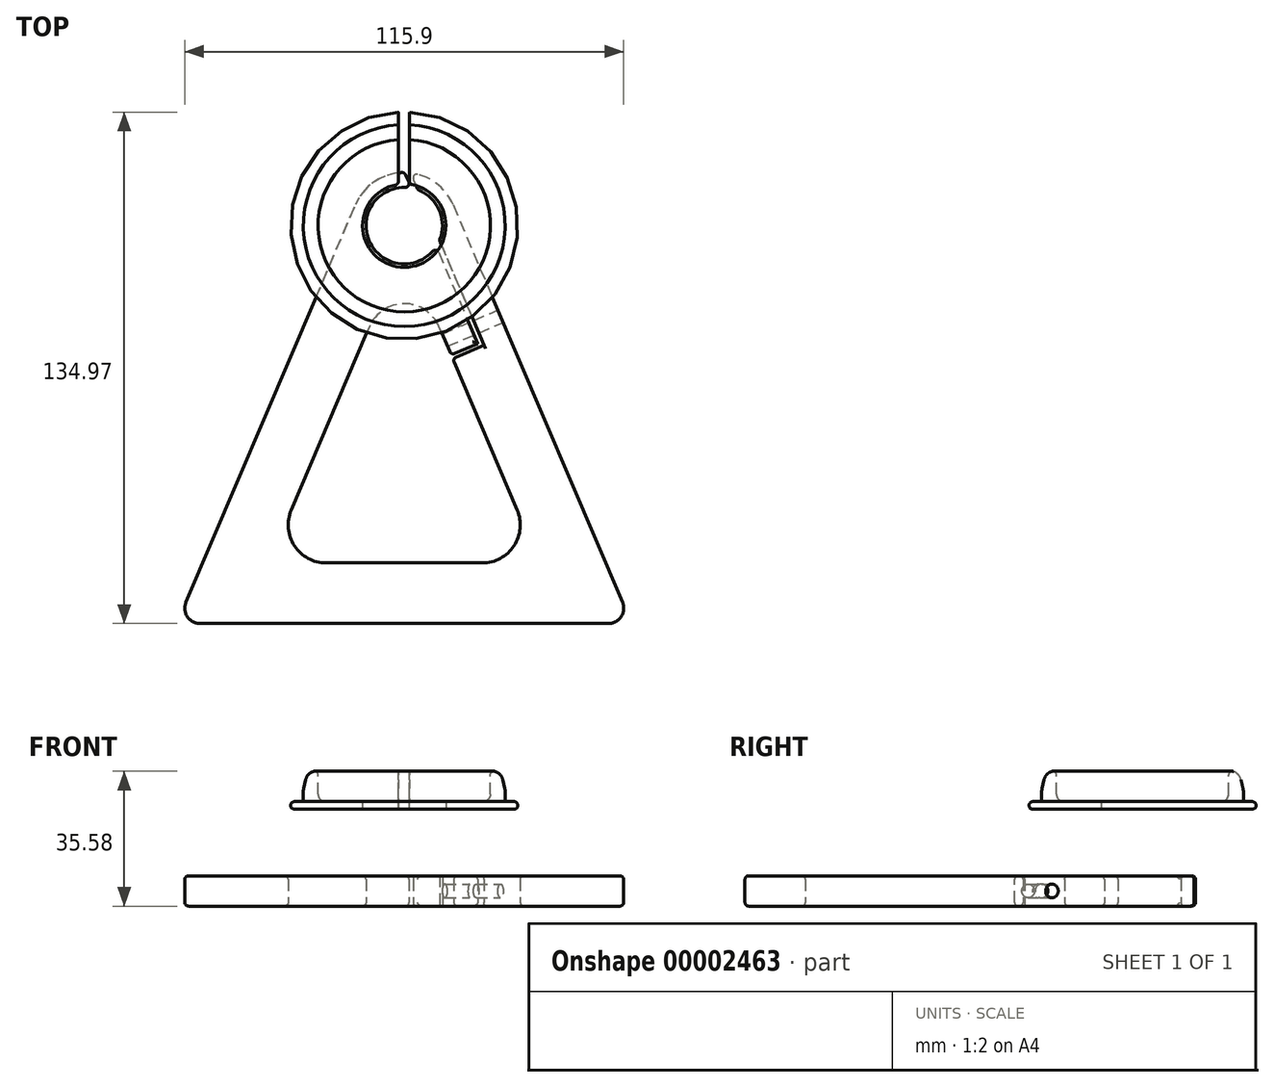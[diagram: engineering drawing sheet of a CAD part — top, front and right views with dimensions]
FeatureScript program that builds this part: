
annotation { "Feature Type Name" : "Feature", "Feature Type Description" : "" }
export const myFeature = defineFeature(function(context is Context, id is Id, definition is map)
    precondition{}
    {
        {
            var Q0;
            Q0=qCreatedBy(makeId("Top.planeOp"),FACE);
            var sketch = newSketch(context, id + "F0", { "sketchPlane" : qUnion([Q0])});
            skLineSegment(sketch, "E0", {"start": v(-53.95, -105) * mm, "end": v(53.95, -105) * mm});
            skArc(sketch, "E1", {"start": v(9.3, -3.95) * mm, "mid": v(-8.9, 4.76) * mm, "end": v(8.45, -5.53) * mm});
            skLineSegment(sketch, "E2", {"start": v(-57.62, -99.43) * mm, "end": v(-12.88, 5.5) * mm});
            skLineSegment(sketch, "E3", {"start": v(12.88, 5.5) * mm, "end": v(57.62, -99.43) * mm});
            skArc(sketch, "E4", {"start": v(12.88, 5.5) * mm, "mid": v(0, 14) * mm, "end": v(-12.88, 5.5) * mm});
            skPoint(sketch, "E5.visualSharp", {"position": v(-60, -105) * mm});
            skArc(sketch, "E5.filletArc", {"start": v(-57.62, -99.43) * mm, "mid": v(-57.28, -103.2) * mm, "end": v(-53.95, -105) * mm});
            skPoint(sketch, "E6.visualSharp", {"position": v(60, -105) * mm});
            skArc(sketch, "E6.filletArc", {"start": v(53.95, -105) * mm, "mid": v(57.28, -103.2) * mm, "end": v(57.62, -99.43) * mm});
            skLineSegment(sketch, "E7", {"start": v(-9.2, -26.67) * mm, "end": v(-29.84, -75.08) * mm});
            skLineSegment(sketch, "E8", {"start": v(-20.65, -89) * mm, "end": v(20.65, -89) * mm});
            skLineSegment(sketch, "E9", {"start": v(29.84, -75.08) * mm, "end": v(9.2, -26.67) * mm});
            skArc(sketch, "E10.filletArc", {"start": v(9.2, -26.67) * mm, "mid": v(0, -20.59) * mm, "end": v(-9.2, -26.67) * mm});
            skPoint(sketch, "E11.visualSharp", {"position": v(-35.78, -89) * mm});
            skArc(sketch, "E11.filletArc", {"start": v(-29.84, -75.08) * mm, "mid": v(-28.99, -84.51) * mm, "end": v(-20.65, -89) * mm});
            skPoint(sketch, "E12.visualSharp", {"position": v(35.78, -89) * mm});
            skArc(sketch, "E12.filletArc", {"start": v(20.65, -89) * mm, "mid": v(28.99, -84.51) * mm, "end": v(29.84, -75.08) * mm});
            skCircle(sketch, "E13", {"center": v(0, 0) * mm, "radius": 100 * mm, "construction": true});
            skLineSegment(sketch, "E14", {"start": v(1.68, 13.9) * mm, "end": v(21.06, -31.55) * mm});
            skLineSegment(sketch, "E15", {"start": v(0.12, 14) * mm, "end": v(19.39, -31.17) * mm});
            skLineSegment(sketch, "E16", {"start": v(12.79, -35.08) * mm, "end": v(21.06, -31.55) * mm});
            skLineSegment(sketch, "E17", {"start": v(12.4, -34.16) * mm, "end": v(19.39, -31.17) * mm});
            skCircle(sketch, "E18", {"center": v(40, -91.8) * mm, "radius": 13.2 * mm, "construction": true});
            skCircle(sketch, "E19", {"center": v(40, -91.8) * mm, "radius": 10 * mm, "construction": true});
            skCircle(sketch, "E20", {"center": v(-40, -91.8) * mm, "radius": 13.2 * mm, "construction": true});
            skCircle(sketch, "E21", {"center": v(-40, -91.8) * mm, "radius": 10.2 * mm, "construction": true});
            skSolve(sketch);
        }
        {
            var Q0;
            Q0=makeQuery(id+"F0.imprint","IMPRINT",FACE,{"disambiguationData":[TD([[makeQuery(id+"F0.imprint","IMPRINT",EDGE,{"derivedFrom":sQuery(id+"F0.wireOp",EDGE,"E0")}),1.0]])]});
            extrude(context, id + "F1", {"entities" : qUnion([Q0]), "depth" : 8 * mm});
        }
        {
            var Q0;
            Q0=makeQuery(id+"F1.opExtrude","SWEPT_FACE",FACE,{"disambiguationData":[OSD([sQuery(id+"F0.wireOp",EDGE,"E3")])]});
            var sketch = newSketch(context, id + "F2", { "sketchPlane" : qUnion([Q0])});
            skCircle(sketch, "E22", {"center": v(-32, 4) * mm, "radius": 1.8 * mm});
            skSolve(sketch);
        }
        {
            var Q0;
            Q0=qSketchRegion(id+"F2",true);
            var Q1;
            {var subQ0=sQuery(id+"F0.wireOp",EDGE,"E9");Q1=makeQuery(id+"F1.opExtrude","SWEPT_FACE",FACE,{"disambiguationData":[OSD([subQ0]),TDD([makeQuery(id+"F0.imprint","IMPRINT",EDGE,{"disambiguationData":[TD([[makeQuery(id+"F0.imprint","INTERSECT",VERTEX,{"derivedFrom":[subQ0,sQuery(id+"F0.wireOp",EDGE,"E10.filletArc")]}),1.0]])],"derivedFrom":subQ0})])]});}
            extrude(context, id + "F3", {"entities" : qUnion([Q0]), "operationType" : NewBodyOperationType.REMOVE, "endBound" : BoundingType.UP_TO_SURFACE, "oppositeDirection" : true, "endBoundEntityFace" : qUnion([Q1]), "depth" : 25 * mm});
        }
        {
            var Q0;
            {var subQ0=sQuery(id+"F0.wireOp",EDGE,"E1");var subQ1=sQuery(id+"F0.wireOp",EDGE,"E15");Q0=makeQuery(id+"F1.opExtrude","CAP_EDGE",EDGE,{"disambiguationData":[OSD([subQ0]),TDD([makeQuery(id+"F0.imprint","IMPRINT",EDGE,{"disambiguationData":[TD([[makeQuery(id+"F0.imprint","INTERSECT",VERTEX,{"disambiguationData":[OD(0.0)],"derivedFrom":[subQ0,subQ1]}),1.0]])],"derivedFrom":subQ0})])],"isStart":false});}
            var Q1;
            {var subQ0=sQuery(id+"F0.wireOp",EDGE,"E4");Q1=makeQuery(id+"F1.opExtrude","CAP_EDGE",EDGE,{"disambiguationData":[OSD([subQ0]),TDD([makeQuery(id+"F0.imprint","IMPRINT",EDGE,{"disambiguationData":[TD([[makeQuery(id+"F0.imprint","INTERSECT",VERTEX,{"derivedFrom":[sQuery(id+"F0.wireOp",EDGE,"E2"),subQ0]}),1.0]])],"derivedFrom":subQ0})])],"isStart":false});}
            var Q2;
            {var subQ0=sQuery(id+"F0.wireOp",EDGE,"E15");Q2=makeQuery(id+"F1.opExtrude","CAP_EDGE",EDGE,{"disambiguationData":[OSD([subQ0]),TDD([makeQuery(id+"F0.imprint","IMPRINT",EDGE,{"disambiguationData":[TD([[makeQuery(id+"F0.imprint","INTERSECT",VERTEX,{"disambiguationData":[OD(0.0)],"derivedFrom":[sQuery(id+"F0.wireOp",EDGE,"E1"),subQ0]}),-1.0]])],"derivedFrom":subQ0})])],"isStart":false});}
            var Q3;
            Q3=makeQuery(id+"F1.opExtrude","CAP_EDGE",EDGE,{"disambiguationData":[OSD([sQuery(id+"F0.wireOp",EDGE,"E17")])],"isStart":false});
            var Q4;
            Q4=makeQuery(id+"F1.opExtrude","CAP_EDGE",EDGE,{"disambiguationData":[OSD([sQuery(id+"F0.wireOp",EDGE,"E10.filletArc")])],"isStart":false});
            var Q5;
            {var subQ0=sQuery(id+"F0.wireOp",EDGE,"E9");Q5=makeQuery(id+"F1.opExtrude","CAP_EDGE",EDGE,{"disambiguationData":[OSD([subQ0]),TDD([makeQuery(id+"F0.imprint","IMPRINT",EDGE,{"disambiguationData":[TD([[makeQuery(id+"F0.imprint","INTERSECT",VERTEX,{"derivedFrom":[subQ0,sQuery(id+"F0.wireOp",EDGE,"E10.filletArc")]}),1.0]])],"derivedFrom":subQ0})])],"isStart":false});}
            var Q6;
            {var subQ0=sQuery(id+"F0.wireOp",EDGE,"E1");var subQ1=sQuery(id+"F0.wireOp",EDGE,"E14");Q6=makeQuery(id+"F1.opExtrude","CAP_EDGE",EDGE,{"disambiguationData":[OSD([subQ0]),TDD([makeQuery(id+"F0.imprint","IMPRINT",EDGE,{"disambiguationData":[TD([[makeQuery(id+"F0.imprint","INTERSECT",VERTEX,{"disambiguationData":[OD(0.0)],"derivedFrom":[subQ0,subQ1]}),-1.0]])],"derivedFrom":subQ0})])],"isStart":false});}
            var Q7;
            {var subQ0=sQuery(id+"F0.wireOp",EDGE,"E1");var subQ1=sQuery(id+"F0.wireOp",EDGE,"E15");Q7=makeQuery(id+"F1.opExtrude","CAP_EDGE",EDGE,{"disambiguationData":[OSD([subQ0]),TDD([makeQuery(id+"F0.imprint","IMPRINT",EDGE,{"disambiguationData":[TD([[makeQuery(id+"F0.imprint","INTERSECT",VERTEX,{"disambiguationData":[OD(0.0)],"derivedFrom":[subQ0,subQ1]}),1.0]])],"derivedFrom":subQ0})])],"isStart":true});}
            var Q8;
            {var subQ0=sQuery(id+"F0.wireOp",EDGE,"E15");Q8=makeQuery(id+"F1.opExtrude","CAP_EDGE",EDGE,{"disambiguationData":[OSD([subQ0]),TDD([makeQuery(id+"F0.imprint","IMPRINT",EDGE,{"disambiguationData":[TD([[makeQuery(id+"F0.imprint","INTERSECT",VERTEX,{"disambiguationData":[OD(0.0)],"derivedFrom":[sQuery(id+"F0.wireOp",EDGE,"E1"),subQ0]}),-1.0]])],"derivedFrom":subQ0})])],"isStart":true});}
            var Q9;
            Q9=makeQuery(id+"F1.opExtrude","CAP_EDGE",EDGE,{"disambiguationData":[OSD([sQuery(id+"F0.wireOp",EDGE,"E17")])],"isStart":true});
            var Q10;
            {var subQ0=sQuery(id+"F0.wireOp",EDGE,"E9");Q10=makeQuery(id+"F1.opExtrude","CAP_EDGE",EDGE,{"disambiguationData":[OSD([subQ0]),TDD([makeQuery(id+"F0.imprint","IMPRINT",EDGE,{"disambiguationData":[TD([[makeQuery(id+"F0.imprint","INTERSECT",VERTEX,{"derivedFrom":[subQ0,sQuery(id+"F0.wireOp",EDGE,"E10.filletArc")]}),1.0]])],"derivedFrom":subQ0})])],"isStart":true});}
            var Q11;
            {var subQ0=sQuery(id+"F0.wireOp",EDGE,"E14");Q11=makeQuery(id+"F1.opExtrude","CAP_EDGE",EDGE,{"disambiguationData":[OSD([subQ0]),TDD([makeQuery(id+"F0.imprint","IMPRINT",EDGE,{"disambiguationData":[TD([[makeQuery(id+"F0.imprint","INTERSECT",VERTEX,{"disambiguationData":[OD(0.0)],"derivedFrom":[sQuery(id+"F0.wireOp",EDGE,"E1"),subQ0]}),-1.0]])],"derivedFrom":subQ0})])],"isStart":true});}
            var Q12;
            Q12=makeQuery(id+"F1.opExtrude","CAP_EDGE",EDGE,{"disambiguationData":[OSD([sQuery(id+"F0.wireOp",EDGE,"E16")])],"isStart":true});
            var Q13;
            Q13=makeQuery(id+"F1.opExtrude","CAP_EDGE",EDGE,{"disambiguationData":[OSD([sQuery(id+"F0.wireOp",EDGE,"E3")])],"isStart":true});
            var Q14;
            {var subQ0=sQuery(id+"F0.wireOp",EDGE,"E1");var subQ1=sQuery(id+"F0.wireOp",EDGE,"E14");Q14=makeQuery(id+"F1.opExtrude","CAP_EDGE",EDGE,{"disambiguationData":[OSD([subQ0]),TDD([makeQuery(id+"F0.imprint","IMPRINT",EDGE,{"disambiguationData":[TD([[makeQuery(id+"F0.imprint","INTERSECT",VERTEX,{"disambiguationData":[OD(0.0)],"derivedFrom":[subQ0,subQ1]}),-1.0]])],"derivedFrom":subQ0})])],"isStart":true});}
            var Q15;
            {var subQ0=sQuery(id+"F0.wireOp",EDGE,"E1");var subQ1=sQuery(id+"F0.wireOp",EDGE,"E15");Q15=makeQuery(id+"F1.opExtrude","SWEPT_EDGE",EDGE,{"disambiguationData":[OSD([subQ0,subQ1]),TDD([makeQuery(id+"F0.imprint","INTERSECT",VERTEX,{"disambiguationData":[OD(0.0)],"derivedFrom":[subQ0,subQ1]})])]});}
            var Q16;
            {var subQ0=sQuery(id+"F0.wireOp",EDGE,"E1");var subQ1=sQuery(id+"F0.wireOp",EDGE,"E15");Q16=makeQuery(id+"F1.opExtrude","SWEPT_EDGE",EDGE,{"disambiguationData":[OSD([subQ0,subQ1]),TDD([makeQuery(id+"F0.imprint","INTERSECT",VERTEX,{"disambiguationData":[OD(1.0)],"derivedFrom":[subQ0,subQ1]})])]});}
            var Q17;
            Q17=makeQuery(id+"F1.opExtrude","SWEPT_EDGE",EDGE,{"disambiguationData":[OSD([sQuery(id+"F0.wireOp",EDGE,"E4"),sQuery(id+"F0.wireOp",EDGE,"E15")])]});
            var Q18;
            {var subQ0=sQuery(id+"F0.wireOp",EDGE,"E15");Q18=makeQuery(id+"F1.opExtrude","CAP_EDGE",EDGE,{"disambiguationData":[OSD([subQ0]),TDD([makeQuery(id+"F0.imprint","IMPRINT",EDGE,{"disambiguationData":[TD([[makeQuery(id+"F0.imprint","INTERSECT",VERTEX,{"derivedFrom":[sQuery(id+"F0.wireOp",EDGE,"E4"),subQ0]}),-1.0]])],"derivedFrom":subQ0})])],"isStart":false});}
            var Q19;
            {var subQ0=sQuery(id+"F0.wireOp",EDGE,"E14");Q19=makeQuery(id+"F1.opExtrude","CAP_EDGE",EDGE,{"disambiguationData":[OSD([subQ0]),TDD([makeQuery(id+"F0.imprint","IMPRINT",EDGE,{"disambiguationData":[TD([[makeQuery(id+"F0.imprint","INTERSECT",VERTEX,{"derivedFrom":[sQuery(id+"F0.wireOp",EDGE,"E4"),subQ0]}),-1.0]])],"derivedFrom":subQ0})])],"isStart":false});}
            var Q20;
            Q20=makeQuery(id+"F1.opExtrude","SWEPT_EDGE",EDGE,{"disambiguationData":[OSD([sQuery(id+"F0.wireOp",EDGE,"E4"),sQuery(id+"F0.wireOp",EDGE,"E14")])]});
            var Q21;
            {var subQ0=sQuery(id+"F0.wireOp",EDGE,"E14");Q21=makeQuery(id+"F1.opExtrude","CAP_EDGE",EDGE,{"disambiguationData":[OSD([subQ0]),TDD([makeQuery(id+"F0.imprint","IMPRINT",EDGE,{"disambiguationData":[TD([[makeQuery(id+"F0.imprint","INTERSECT",VERTEX,{"disambiguationData":[OD(0.0)],"derivedFrom":[sQuery(id+"F0.wireOp",EDGE,"E1"),subQ0]}),-1.0]])],"derivedFrom":subQ0})])],"isStart":false});}
            var Q22;
            {var subQ0=sQuery(id+"F0.wireOp",EDGE,"E1");var subQ1=sQuery(id+"F0.wireOp",EDGE,"E14");Q22=makeQuery(id+"F1.opExtrude","SWEPT_EDGE",EDGE,{"disambiguationData":[OSD([subQ0,subQ1]),TDD([makeQuery(id+"F0.imprint","INTERSECT",VERTEX,{"disambiguationData":[OD(0.0)],"derivedFrom":[subQ0,subQ1]})])]});}
            var Q23;
            {var subQ0=sQuery(id+"F0.wireOp",EDGE,"E15");Q23=makeQuery(id+"F1.opExtrude","CAP_EDGE",EDGE,{"disambiguationData":[OSD([subQ0]),TDD([makeQuery(id+"F0.imprint","IMPRINT",EDGE,{"disambiguationData":[TD([[makeQuery(id+"F0.imprint","INTERSECT",VERTEX,{"derivedFrom":[sQuery(id+"F0.wireOp",EDGE,"E4"),subQ0]}),-1.0]])],"derivedFrom":subQ0})])],"isStart":true});}
            var Q24;
            {var subQ0=sQuery(id+"F0.wireOp",EDGE,"E14");Q24=makeQuery(id+"F1.opExtrude","CAP_EDGE",EDGE,{"disambiguationData":[OSD([subQ0]),TDD([makeQuery(id+"F0.imprint","IMPRINT",EDGE,{"disambiguationData":[TD([[makeQuery(id+"F0.imprint","INTERSECT",VERTEX,{"derivedFrom":[sQuery(id+"F0.wireOp",EDGE,"E4"),subQ0]}),-1.0]])],"derivedFrom":subQ0})])],"isStart":true});}
            var Q25;
            {var subQ0=sQuery(id+"F0.wireOp",EDGE,"E1");var subQ1=sQuery(id+"F0.wireOp",EDGE,"E14");Q25=makeQuery(id+"F1.opExtrude","SWEPT_EDGE",EDGE,{"disambiguationData":[OSD([subQ0,subQ1]),TDD([makeQuery(id+"F0.imprint","INTERSECT",VERTEX,{"disambiguationData":[OD(1.0)],"derivedFrom":[subQ0,subQ1]})])]});}
            var Q26;
            Q26=makeQuery(id+"F1.opExtrude","CAP_EDGE",EDGE,{"disambiguationData":[OSD([sQuery(id+"F0.wireOp",EDGE,"E16")])],"isStart":false});
            var Q27;
            Q27=makeQuery(id+"F1.opExtrude","SWEPT_EDGE",EDGE,{"disambiguationData":[OSD([sQuery(id+"F0.wireOp",EDGE,"E9"),sQuery(id+"F0.wireOp",EDGE,"E16")])]});
            var Q28;
            Q28=makeQuery(id+"F1.opExtrude","SWEPT_EDGE",EDGE,{"disambiguationData":[OSD([sQuery(id+"F0.wireOp",EDGE,"E9"),sQuery(id+"F0.wireOp",EDGE,"E17")])]});
            fillet(context, id + "F4", {"entities" : qUnion([Q0, Q1, Q2, Q3, Q4, Q5, Q6, Q7, Q8, Q9, Q10, Q11, Q12, Q13, Q14, Q15, Q16, Q17, Q18, Q19, Q20, Q21, Q22, Q23, Q24, Q25, Q26, Q27, Q28]), "radius" : 1 * mm, "tangentPropagation" : true, "allowEdgeOverflow" : false});
        }
        {
            var Q0;
            Q0=makeQuery(id+"F3.boolean.opBoolean","COPY",EDGE,{"derivedFrom":makeQuery(id+"F3.opExtrude","CAP_EDGE",EDGE,{"disambiguationData":[OSD([sQuery(id+"F2.wireOp",EDGE,"E22")])],"isStart":true})});
            var Q1;
            {var subQ0=sQuery(id+"F0.wireOp",EDGE,"E14");Q1=makeQuery(id+"F3.boolean.opBoolean","INTERSECT",EDGE,{"derivedFrom":[makeQuery(id+"F1.opExtrude","SWEPT_FACE",FACE,{"disambiguationData":[OSD([subQ0]),TDD([makeQuery(id+"F0.imprint","IMPRINT",EDGE,{"disambiguationData":[TD([[makeQuery(id+"F0.imprint","INTERSECT",VERTEX,{"disambiguationData":[OD(0.0)],"derivedFrom":[sQuery(id+"F0.wireOp",EDGE,"E1"),subQ0]}),-1.0]])],"derivedFrom":subQ0})])]}),makeQuery(id+"F3.opExtrude","SWEPT_FACE",FACE,{"disambiguationData":[OSD([sQuery(id+"F2.wireOp",EDGE,"E22")])]})]});}
            var Q2;
            {var subQ0=sQuery(id+"F0.wireOp",EDGE,"E15");Q2=makeQuery(id+"F3.boolean.opBoolean","INTERSECT",EDGE,{"derivedFrom":[makeQuery(id+"F1.opExtrude","SWEPT_FACE",FACE,{"disambiguationData":[OSD([subQ0]),TDD([makeQuery(id+"F0.imprint","IMPRINT",EDGE,{"disambiguationData":[TD([[makeQuery(id+"F0.imprint","INTERSECT",VERTEX,{"disambiguationData":[OD(0.0)],"derivedFrom":[sQuery(id+"F0.wireOp",EDGE,"E1"),subQ0]}),-1.0]])],"derivedFrom":subQ0})])]}),makeQuery(id+"F3.opExtrude","SWEPT_FACE",FACE,{"disambiguationData":[OSD([sQuery(id+"F2.wireOp",EDGE,"E22")])]})]});}
            var Q3;
            Q3=makeQuery(id+"F3.boolean.opBoolean","COPY",EDGE,{"derivedFrom":makeQuery(id+"F3.opExtrude","CAP_EDGE",EDGE,{"disambiguationData":[OSD([sQuery(id+"F2.wireOp",EDGE,"E22")])],"isStart":false})});
            fillet(context, id + "F5", {"entities" : qUnion([Q0, Q1, Q2, Q3]), "radius" : 0.6 * mm, "tangentPropagation" : true, "allowEdgeOverflow" : false});
        }
        {
            var Q0;
            Q0=qCreatedBy(makeId("Right.planeOp"),FACE);
            var sketch = newSketch(context, id + "F6", { "sketchPlane" : qUnion([Q0])});
            skLineSegment(sketch, "E23", {"start": v(29, 25.58) * mm, "end": v(0, 25.58) * mm});
            skPoint(sketch, "E24.visualSharp", {"position": v(24.99, 35.56) * mm});
            skArc(sketch, "E24.filletArc", {"start": v(26.02, 33.34) * mm, "mid": v(25.32, 34.7) * mm, "end": v(24.04, 35.53) * mm});
            skLineSegment(sketch, "E25", {"start": v(0, 30.58) * mm, "end": v(26.65, 30.58) * mm, "construction": true});
            skArc(sketch, "E26", {"start": v(24.04, 35.53) * mm, "mid": v(23.15, 35.4) * mm, "end": v(22.74, 34.6) * mm});
            skLineSegment(sketch, "E27", {"start": v(26.58, 35.58) * mm, "end": v(20.64, 35.58) * mm, "construction": true});
            skLineSegment(sketch, "E28.bottom", {"start": v(27.45, 27.58) * mm, "end": v(29, 27.58) * mm});
            skPoint(sketch, "E29.visualSharp", {"position": v(23.1, 27.58) * mm});
            skArc(sketch, "E29.filletArc", {"start": v(26.65, 28.38) * mm, "mid": v(26.88, 27.81) * mm, "end": v(27.45, 27.58) * mm});
            skArc(sketch, "E30", {"start": v(29, 25.58) * mm, "mid": v(30, 26.58) * mm, "end": v(29, 27.58) * mm});
            skLineSegment(sketch, "E31", {"start": v(20.74, 27.58) * mm, "end": v(0, 27.58) * mm});
            skLineSegment(sketch, "E32", {"start": v(0, 27.58) * mm, "end": v(0, 25.58) * mm});
            skLineSegment(sketch, "E33", {"start": v(22.74, 34.6) * mm, "end": v(22.74, 29.58) * mm});
            skLineSegment(sketch, "E34", {"start": v(23.73, 34.6) * mm, "end": v(22.74, 34.6) * mm, "construction": true});
            skPoint(sketch, "E35.visualSharp", {"position": v(22.74, 27.58) * mm});
            skArc(sketch, "E35.filletArc", {"start": v(20.74, 27.58) * mm, "mid": v(22.15, 28.16) * mm, "end": v(22.74, 29.58) * mm});
            skLineSegment(sketch, "E36", {"start": v(26.65, 28.38) * mm, "end": v(26.65, 30.13) * mm});
            skLineSegment(sketch, "E37", {"start": v(26.02, 33.34) * mm, "end": v(26.55, 31.02) * mm});
            skPoint(sketch, "E38.visualSharp", {"position": v(26.65, 30.58) * mm});
            skArc(sketch, "E38.filletArc", {"start": v(26.65, 30.13) * mm, "mid": v(26.63, 30.57) * mm, "end": v(26.55, 31.02) * mm});
            skSolve(sketch);
        }
        {
            var Q0;
            Q0=qSketchRegion(id+"F6",true);
            var Q1;
            Q1=sQuery(id+"F6.wireOp",EDGE,"E32");
            revolve(context, id + "F7", {"entities" : qUnion([Q0]), "axis" : qUnion([Q1]), "revolveType" : RevolveType.FULL});
        }
        {
            var Q0;
            Q0=makeQuery(id+"F7.opRevolve","SWEPT_FACE",FACE,{"disambiguationData":[OSD([sQuery(id+"F6.wireOp",EDGE,"E23")])]});
            var sketch = newSketch(context, id + "F8", { "sketchPlane" : qUnion([Q0])});
            skCircle(sketch, "E39", {"center": v(0, 0) * mm, "radius": 11 * mm});
            skLineSegment(sketch, "E40.rect.top", {"start": v(1.41, -38.94) * mm, "end": v(-1.59, -38.94) * mm});
            skLineSegment(sketch, "E40.rect.left", {"start": v(1.41, -10.9) * mm, "end": v(1.41, -38.94) * mm});
            skLineSegment(sketch, "E40.rect.right", {"start": v(-1.59, -10.88) * mm, "end": v(-1.59, -38.94) * mm});
            skPoint(sketch, "E40.rect.middle", {"position": v(0, -36.15) * mm});
            skSolve(sketch);
        }
        {
            var Q0;
            Q0=qSketchRegion(id+"F8",true);
            var Q1;
            Q1=makeQuery(id+"F7.opRevolve","SWEPT_FACE",FACE,{"disambiguationData":[OSD([sQuery(id+"F6.wireOp",EDGE,"E23")])]});
            extrude(context, id + "F9", {"entities" : qUnion([Q0]), "operationType" : NewBodyOperationType.REMOVE, "endBound" : BoundingType.UP_TO_BODY, "oppositeDirection" : true, "endBoundEntityBody" : qUnion([Q1]), "depth" : 25 * mm});
        }
        {
            var Q0;
            Q0=makeQuery(id+"F9.boolean.opBoolean","COPY",EDGE,{"derivedFrom":makeQuery(id+"F9.opExtrude","CAP_EDGE",EDGE,{"disambiguationData":[OSD([sQuery(id+"F8.wireOp",EDGE,"E39")])],"isStart":false})});
            var Q1;
            Q1=makeQuery(id+"F9.boolean.opBoolean","COPY",EDGE,{"derivedFrom":makeQuery(id+"F9.opExtrude","CAP_EDGE",EDGE,{"disambiguationData":[OSD([sQuery(id+"F8.wireOp",EDGE,"E40.rect.right")]),topologyDisambiguationEdgeConnected([makeQuery(id+"F7.opRevolve","SWEPT_FACE",FACE,{"disambiguationData":[OSD([sQuery(id+"F6.wireOp",EDGE,"E31")])]})])],"isStart":false})});
            var Q2;
            Q2=makeQuery(id+"F9.boolean.opBoolean","COPY",EDGE,{"derivedFrom":makeQuery(id+"F9.opExtrude","CAP_EDGE",EDGE,{"disambiguationData":[OSD([sQuery(id+"F8.wireOp",EDGE,"E40.rect.right")]),topologyDisambiguationEdgeConnected([makeQuery(id+"F7.opRevolve","SWEPT_FACE",FACE,{"disambiguationData":[OSD([sQuery(id+"F6.wireOp",EDGE,"E26")])]})])],"isStart":false})});
            var Q3;
            Q3=makeQuery(id+"F9.boolean.opBoolean","COPY",EDGE,{"derivedFrom":makeQuery(id+"F9.opExtrude","CAP_EDGE",EDGE,{"disambiguationData":[OSD([sQuery(id+"F8.wireOp",EDGE,"E40.rect.left")]),topologyDisambiguationEdgeConnected([makeQuery(id+"F7.opRevolve","SWEPT_FACE",FACE,{"disambiguationData":[OSD([sQuery(id+"F6.wireOp",EDGE,"E31")])]})])],"isStart":false})});
            var Q4;
            {var subQ0=sQuery(id+"F8.wireOp",EDGE,"E40.rect.left");Q4=makeQuery(id+"F9.boolean.opBoolean","COPY",EDGE,{"derivedFrom":makeQuery(id+"F9.opExtrude","TWEAK_EDGE",EDGE,{"derivedFrom":[makeQuery(id+"F7.opRevolve","SWEPT_FACE",FACE,{"disambiguationData":[OSD([sQuery(id+"F6.wireOp",EDGE,"a11749e0-a4c9-4a4f-9974-4c692c2e9dff.5")])]}),makeQuery(id+"F8.imprint","IMPRINT",EDGE,{"disambiguationData":[TD([[makeQuery(id+"F8.imprint","INTERSECT",VERTEX,{"derivedFrom":[sQuery(id+"F8.wireOp",EDGE,"E39"),subQ0]}),-1.0]])],"derivedFrom":subQ0}),makeQuery(id+"F8.imprint","IMPRINT",EDGE,{"disambiguationData":[TD([[makeQuery(id+"F8.imprint","INTERSECT",VERTEX,{"derivedFrom":[sQuery(id+"F8.wireOp",EDGE,"E40.rect.top"),subQ0]}),1.0]])],"derivedFrom":subQ0})]})});}
            var Q5;
            Q5=makeQuery(id+"F9.boolean.opBoolean","COPY",EDGE,{"derivedFrom":makeQuery(id+"F9.opExtrude","CAP_EDGE",EDGE,{"disambiguationData":[OSD([sQuery(id+"F8.wireOp",EDGE,"E40.rect.left")]),topologyDisambiguationEdgeConnected([makeQuery(id+"F7.opRevolve","SWEPT_FACE",FACE,{"disambiguationData":[OSD([sQuery(id+"F6.wireOp",EDGE,"E26")])]})])],"isStart":false})});
            var Q6;
            Q6=makeQuery(id+"F9.boolean.opBoolean","COPY",EDGE,{"derivedFrom":makeQuery(id+"F9.opExtrude","CAP_EDGE",EDGE,{"disambiguationData":[OSD([sQuery(id+"F8.wireOp",EDGE,"E40.rect.left")]),topologyDisambiguationEdgeConnected([makeQuery(id+"F7.opRevolve","SWEPT_FACE",FACE,{"disambiguationData":[OSD([sQuery(id+"F6.wireOp",EDGE,"E28.bottom")])]})])],"isStart":false})});
            var Q7;
            Q7=makeQuery(id+"F9.boolean.opBoolean","COPY",EDGE,{"derivedFrom":makeQuery(id+"F9.opExtrude","SWEPT_EDGE",EDGE,{"disambiguationData":[OSD([sQuery(id+"F8.wireOp",EDGE,"E39"),sQuery(id+"F8.wireOp",EDGE,"E40.rect.left")])]})});
            var Q8;
            Q8=makeQuery(id+"F9.boolean.opBoolean","COPY",EDGE,{"derivedFrom":makeQuery(id+"F9.opExtrude","SWEPT_EDGE",EDGE,{"disambiguationData":[OSD([sQuery(id+"F8.wireOp",EDGE,"E39"),sQuery(id+"F8.wireOp",EDGE,"E40.rect.right")])]})});
            var Q9;
            Q9=makeQuery(id+"F9.boolean.opBoolean","COPY",EDGE,{"derivedFrom":makeQuery(id+"F9.opExtrude","CAP_EDGE",EDGE,{"disambiguationData":[OSD([sQuery(id+"F8.wireOp",EDGE,"E39")])],"isStart":true})});
            fillet(context, id + "F10", {"entities" : qUnion([Q0, Q1, Q2, Q3, Q4, Q5, Q6, Q7, Q8, Q9]), "radius" : 0.8 * mm, "tangentPropagation" : true, "allowEdgeOverflow" : false});
        }
    });
